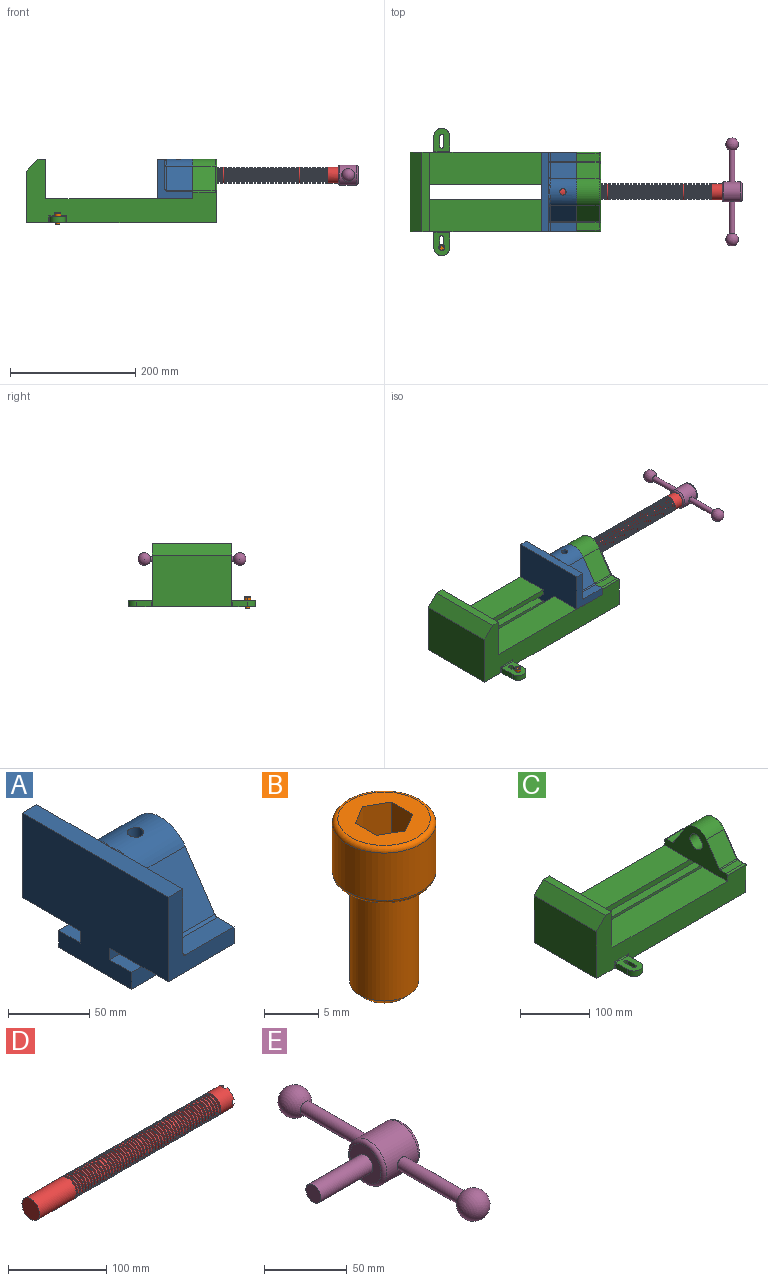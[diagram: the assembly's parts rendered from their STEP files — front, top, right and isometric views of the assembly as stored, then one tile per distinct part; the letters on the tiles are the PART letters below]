
ASSEMBLY  parts=5 mates=5
PART A: 36 faces, bbox 57.2x127x89 mm
  f0: plane 57.15x50.8mm, normal (0,0,-1), area 2903.2mm2, adj f6,f9,f10,f23
  f1: cylinder r=12.7mm len=44.45mm, axis (1,0,0), area 3464.3mm2, adj f6,f15,f16
  f2: plane 41.91x14.52mm, normal (0,0,1), area 608.5mm2, adj f6,f11,f24,f25
  f3: plane 51.86x48.26mm, normal (1,0,0), area 1495.7mm2, adj f8,f10,f31,f33,f35
  f4: plane 51.86x48.26mm, normal (1,0,0), area 1495.7mm2, adj f8,f11,f24,f28,f29
  f5: plane 57.15x50.8mm, normal (0,0,-1), area 2903.2mm2, adj f6,f9,f11,f22
  f6: plane 127x85.09mm, normal (1,0,0), area 5190.6mm2, adj f0,f1,f2,f5,f7,f10,f11,f12
  f7: plane 41.91x14.52mm, normal (0,0,1), area 608.5mm2, adj f6,f10,f30,f31
  f8: plane 127x12.7mm, normal (0,0,1), area 1612.9mm2, adj f3,f4,f9,f10,f11,f26,f34
  f9: plane 127x85.09mm, normal (-1,0,0), area 9096.8mm2, adj f0,f5,f8,f10,f11,f17,f18,f19
  f10: plane 63.5x57.15mm, normal (0,-1,0), area 1372.3mm2, adj f0,f3,f6,f7,f8,f9,f31
  f11: plane 63.5x57.15mm, normal (0,1,0), area 1372.3mm2, adj f2,f4,f5,f6,f8,f9,f24
  f12: plane 41.91x38.43mm, normal (0,-0.83,0.56), area 1939.2mm2, adj f6,f13,f30,f33
  f13: cylinder r=25.4mm len=44.45mm, axis (1,0,0), area 2026.5mm2, adj f6,f12,f14,f16,f26,f28,f34,f35
  f14: plane 41.91x38.43mm, normal (0,0.83,0.56), area 1939.2mm2, adj f6,f13,f25,f29
  f15: plane 25.4x25.4mm, normal (1,0,0), area 506.7mm2, adj f1
  f16: cylinder r=5.08mm len=13.76mm, axis (0,0,1), area 414mm2, adj f1,f13
  f17: plane 57.15x19.05mm, normal (0,0,1), area 1088.7mm2, adj f6,f9,f18,f23
  f18: plane 57.15x12.7mm, normal (0,-1,0), area 725.8mm2, adj f6,f9,f17,f19
  f19: plane 63.5x57.15mm, normal (0,0,-1), area 3629mm2, adj f6,f9,f18,f20
  f20: plane 57.15x12.7mm, normal (0,1,0), area 725.8mm2, adj f6,f9,f19,f21
  f21: plane 57.15x19.05mm, normal (0,0,1), area 1088.7mm2, adj f6,f9,f20,f22
  f22: plane 57.15x8.89mm, normal (0,1,0), area 508.1mm2, adj f5,f6,f9,f21
  f23: plane 57.15x8.89mm, normal (0,-1,0), area 508.1mm2, adj f0,f6,f9,f17
  f24: cylinder r=2.54mm len=14.52mm, axis (0,-1,0), area 57.9mm2, adj f2,f4,f11,f27
  f25: cylinder r=2.54mm len=41.91mm, axis (1,0,0), area 104.3mm2, adj f2,f6,f14,f27
  f26: bspline ~12.24x2.8mm, area 20.9mm2, adj f8,f13,f28
  f27: sphere r=2.54mm, area 6.3mm2, adj f24,f25,f29
  f28: torus R=27.94mm, axis (1,0,0), area 57.8mm2, adj f4,f13,f26,f29
  f29: cylinder r=2.54mm len=39.84mm, axis (0,-0.56,0.83), area 184.6mm2, adj f4,f14,f27,f28
  f30: cylinder r=2.54mm len=41.91mm, axis (1,0,0), area 104.3mm2, adj f6,f7,f12,f32
  f31: cylinder r=2.54mm len=14.52mm, axis (0,-1,0), area 57.9mm2, adj f3,f7,f10,f32
  f32: sphere r=2.54mm, area 6.3mm2, adj f30,f31,f33
  f33: cylinder r=2.54mm len=39.84mm, axis (0,-0.56,-0.83), area 184.6mm2, adj f3,f12,f32,f35
  f34: bspline ~12.24x2.8mm, area 20.9mm2, adj f8,f13,f35
  f35: torus R=27.94mm, axis (1,0,0), area 57.8mm2, adj f3,f13,f33,f34
PART B: 15 faces, bbox 10.3x10.3x19.1 mm
  f0: plane 8.51x8.51mm, normal (0,0,1), area 37.2mm2, adj f5,f6,f7,f8,f9,f10,f14
  f1: cylinder r=3.17mm len=11.94mm, axis (0,0,1), area 238.2mm2, adj f4,f12
  f2: plane 4.83x4.83mm, normal (0,0,-1), area 18.3mm2, adj f12
  f3: cylinder r=4.76mm len=9.53mm, axis (0,0,-1), area 159.6mm2, adj f13,f14
  f4: plane 8.51x8.51mm, normal (0,0,-1), area 25.2mm2, adj f1,f13
  f5: plane 4.83x2.38mm, normal (-0.5,-0.87,0), area 13.3mm2, adj f0,f6,f10,f11
  f6: plane 4.83x2.38mm, normal (0.5,-0.87,0), area 13.3mm2, adj f0,f5,f7,f11
  f7: plane 4.83x2.75mm, normal (1,0,0), area 13.3mm2, adj f0,f6,f8,f11
  f8: plane 4.83x2.38mm, normal (0.5,0.87,0), area 13.3mm2, adj f0,f7,f9,f11
  f9: plane 4.83x2.38mm, normal (-0.5,0.87,0), area 13.3mm2, adj f0,f8,f10,f11
  f10: plane 4.83x2.75mm, normal (-1,0,0), area 13.3mm2, adj f0,f5,f9,f11
  f11: plane 5.5x4.76mm, normal (0,0,1), area 19.6mm2, adj f5,f6,f7,f8,f9,f10
  f12: cone r=3.17mm half-angle=45deg, axis (0,0,1), area 18.9mm2, adj f1,f2
  f13: torus R=4.25mm, axis (0,0,1), area 23mm2, adj f3,f4
  f14: torus R=4.25mm, axis (0,0,1), area 23mm2, adj f0,f3
PART C: 61 faces, bbox 304.8x203.2x103.7 mm
  f0: plane 304.8x101.6mm, normal (0,1,0), area 13520.3mm2, adj f3,f4,f5,f6,f7,f8,f9,f16
  f1: plane 304.8x101.6mm, normal (0,-1,0), area 13520.3mm2, adj f2,f3,f5,f6,f7,f8,f9,f16
  f2: plane 234.95x50.8mm, normal (0,0,1), area 11935.5mm2, adj f1,f5,f16,f26
  f3: plane 127x99.06mm, normal (1,0,0), area 7097.5mm2, adj f0,f1,f9,f14,f17,f18,f19,f20
  f4: plane 234.95x50.8mm, normal (0,0,1), area 11935.5mm2, adj f0,f5,f16,f27
  f5: plane 127x101.6mm, normal (1,0,0), area 9516.1mm2, adj f0,f1,f2,f4,f6,f9,f18,f19
  f6: plane 127x12.7mm, normal (0,0,1), area 1612.9mm2, adj f0,f1,f5,f7
  f7: plane 127x19.05mm, normal (-0.71,0,0.71), area 3421.5mm2, adj f0,f1,f6,f8
  f8: plane 127x82.55mm, normal (-1,0,0), area 10483.8mm2, adj f0,f1,f7,f9
  f9: plane 304.8x203.2mm, normal (0,0,-1), area 33298.3mm2, adj f0,f1,f3,f5,f8,f21,f22,f39
  f10: plane 35.56x11.98mm, normal (0,0,1), area 426mm2, adj f16,f28,f29,f30
  f11: plane 38.43x35.56mm, normal (0,0.83,0.56), area 1645.4mm2, adj f12,f16,f29,f32
  f12: cylinder r=25.4mm len=42.19mm, axis (1,0,0), area 1770.2mm2, adj f11,f13,f16,f33
  f13: plane 38.43x35.56mm, normal (0,-0.83,0.56), area 1645.4mm2, adj f12,f16,f34,f35
  f14: cylinder r=12.7mm len=38.1mm, axis (1,0,0), area 3040.2mm2, adj f3,f16
  f15: plane 35.56x11.98mm, normal (0,0,1), area 426mm2, adj f16,f34,f36,f38
  f16: plane 127x63.5mm, normal (-1,0,0), area 4155.5mm2, adj f0,f1,f2,f4,f10,f11,f12,f13
  f17: plane 38.1x25.4mm, normal (0,0,-1), area 967.7mm2, adj f3,f16,f26,f27
  f18: plane 273.05x19.05mm, normal (0,0,-1), area 5201.6mm2, adj f3,f5,f19,f26
  f19: plane 273.05x12.7mm, normal (0,1,0), area 3467.7mm2, adj f3,f5,f18,f20
  f20: plane 273.05x19.05mm, normal (0,0,1), area 5201.6mm2, adj f3,f5,f19,f21
  f21: plane 273.05x16.51mm, normal (0,1,0), area 4508.1mm2, adj f3,f5,f9,f20
  f22: plane 273.05x16.51mm, normal (0,-1,0), area 4508.1mm2, adj f3,f5,f9,f23
  f23: plane 273.05x19.05mm, normal (0,0,1), area 5201.6mm2, adj f3,f5,f22,f24
  f24: plane 273.05x12.7mm, normal (0,-1,0), area 3467.7mm2, adj f3,f5,f23,f25
  f25: plane 273.05x19.05mm, normal (0,0,-1), area 5201.6mm2, adj f3,f5,f24,f27
  f26: plane 273.05x8.89mm, normal (0,1,0), area 2427.4mm2, adj f2,f3,f5,f17,f18
  f27: plane 273.05x8.89mm, normal (0,-1,0), area 2427.4mm2, adj f3,f4,f5,f17,f25
  f28: cylinder r=2.54mm len=38.1mm, axis (1,0,0), area 148.3mm2, adj f0,f10,f16,f30
  f29: cylinder r=2.54mm len=35.56mm, axis (-1,0,0), area 88.5mm2, adj f10,f11,f16,f31
  f30: cylinder r=2.54mm len=14.52mm, axis (0,1,0), area 54.3mm2, adj f3,f10,f28,f31
  f31: torus R=5.08mm, axis (-1,0,0), area 13.5mm2, adj f3,f29,f30,f32
  f32: cylinder r=2.54mm len=39.84mm, axis (0,0.56,-0.83), area 184.6mm2, adj f3,f11,f31,f33
  f33: torus R=22.86mm, axis (-1,0,0), area 191.4mm2, adj f3,f12,f32,f35
  f34: cylinder r=2.54mm len=35.56mm, axis (-1,0,0), area 88.5mm2, adj f13,f15,f16,f37
  f35: cylinder r=2.54mm len=39.84mm, axis (0,0.56,0.83), area 184.6mm2, adj f3,f13,f33,f37
  f36: cylinder r=2.54mm len=38.1mm, axis (-1,0,0), area 148.3mm2, adj f1,f15,f16,f38
  f37: torus R=5.08mm, axis (-1,0,0), area 13.5mm2, adj f3,f34,f35,f38
  f38: cylinder r=2.54mm len=14.52mm, axis (0,1,0), area 54.3mm2, adj f3,f15,f36,f37
  f39: plane 23.88x9.53mm, normal (-1,0,0), area 227.4mm2, adj f9,f45,f46,f60
  f40: plane 23.88x9.53mm, normal (1,0,0), area 227.4mm2, adj f9,f45,f46,f58
  f41: cylinder r=3.3mm len=9.53mm, axis (0,0,-1), area 98.8mm2, adj f9,f42,f44,f46
  f42: plane 15.62x9.53mm, normal (-1,0,0), area 148.8mm2, adj f9,f41,f43,f46
  f43: cylinder r=3.3mm len=9.53mm, axis (0,0,-1), area 98.8mm2, adj f9,f42,f44,f46
  f44: plane 15.62x9.53mm, normal (1,0,0), area 148.8mm2, adj f9,f41,f43,f46
  f45: cylinder r=12.7mm len=25.4mm, axis (0,0,-1), area 380mm2, adj f9,f39,f40,f46
  f46: plane 36.58x25.4mm, normal (0,0,1), area 722.4mm2, adj f39,f40,f41,f42,f43,f44,f45,f59
  f47: plane 23.88x9.53mm, normal (-1,0,0), area 227.4mm2, adj f9,f53,f54,f56
  f48: plane 23.88x9.53mm, normal (1,0,0), area 227.4mm2, adj f9,f53,f54,f55
  f49: cylinder r=3.3mm len=9.53mm, axis (0,0,-1), area 98.8mm2, adj f9,f50,f52,f54
  f50: plane 15.62x9.53mm, normal (-1,0,0), area 148.8mm2, adj f9,f49,f51,f54
  f51: cylinder r=3.3mm len=9.53mm, axis (0,0,-1), area 98.8mm2, adj f9,f50,f52,f54
  f52: plane 15.62x9.53mm, normal (1,0,0), area 148.8mm2, adj f9,f49,f51,f54
  f53: cylinder r=12.7mm len=25.4mm, axis (0,0,-1), area 380mm2, adj f9,f47,f48,f54
  f54: plane 36.58x25.4mm, normal (0,0,1), area 722.4mm2, adj f47,f48,f49,f50,f51,f52,f53,f57
  f55: cylinder r=1.52mm len=11.05mm, axis (0,0,-1), area 24.1mm2, adj f0,f9,f48,f57
  f56: cylinder r=1.52mm len=11.05mm, axis (0,0,1), area 24.1mm2, adj f0,f9,f47,f57
  f57: cylinder r=1.52mm len=28.45mm, axis (1,0,0), area 63.5mm2, adj f0,f54,f55,f56
  f58: cylinder r=1.52mm len=11.05mm, axis (0,0,1), area 24.1mm2, adj f1,f9,f40,f59
  f59: cylinder r=1.52mm len=28.45mm, axis (-1,0,0), area 63.5mm2, adj f1,f46,f58,f60
  f60: cylinder r=1.52mm len=11.05mm, axis (0,0,-1), area 24.1mm2, adj f1,f9,f39,f59
PART D: 220 faces, bbox 279.4x25.4x25.4 mm
  f0: cylinder r=12.7mm len=25.4mm, axis (-1,0,0), area 1468.2mm2, adj f1,f2,f3,f5,f7,f208,f209,f210
  f1: plane 9.9x9.9mm, normal (1,0,0), area 62.3mm2, adj f0,f4,f213,f216
  f2: plane 9.9x9.9mm, normal (1,0,0), area 62.3mm2, adj f0,f4,f210,f218
  f3: plane 9.9x9.9mm, normal (1,0,0), area 62.3mm2, adj f0,f4,f209,f212
  f4: cylinder r=6.35mm len=25.4mm, axis (1,0,0), area 960.3mm2, adj f1,f2,f3,f5,f6,f208,f209,f210
  f5: plane 9.9x9.9mm, normal (1,0,0), area 62.3mm2, adj f0,f4,f215,f217
  f6: plane 12.7x12.7mm, normal (1,0,0), area 126.7mm2, adj f4
  f7: cone r=12.7mm half-angle=76deg, axis (1,0,0), area 188mm2, adj f0,f9
  f8: cone r=10.16mm half-angle=76deg, axis (-1,0,0), area 188mm2, adj f9,f10
  f9: cylinder r=10.16mm len=20.32mm, axis (1,0,0), area 81.1mm2, adj f7,f8
  f10: cylinder r=12.7mm len=25.4mm, axis (-1,0,0), area 131.7mm2, adj f8,f11
  f11: cone r=12.7mm half-angle=76deg, axis (1,0,0), area 188mm2, adj f10,f13
  f12: cone r=10.16mm half-angle=76deg, axis (-1,0,0), area 188mm2, adj f13,f14
  f13: cylinder r=10.16mm len=20.32mm, axis (1,0,0), area 81.1mm2, adj f11,f12
  f14: cylinder r=12.7mm len=25.4mm, axis (-1,0,0), area 131.7mm2, adj f12,f15
  f15: cone r=12.7mm half-angle=76deg, axis (1,0,0), area 188mm2, adj f14,f17
  f16: cone r=10.16mm half-angle=76deg, axis (-1,0,0), area 188mm2, adj f17,f18
  f17: cylinder r=10.16mm len=20.32mm, axis (1,0,0), area 81.1mm2, adj f15,f16
  f18: cylinder r=12.7mm len=25.4mm, axis (-1,0,0), area 131.7mm2, adj f16,f19
  f19: cone r=12.7mm half-angle=76deg, axis (1,0,0), area 188mm2, adj f18,f21
  f20: cone r=10.16mm half-angle=76deg, axis (-1,0,0), area 188mm2, adj f21,f22
  f21: cylinder r=10.16mm len=20.32mm, axis (1,0,0), area 81.1mm2, adj f19,f20
  f22: cylinder r=12.7mm len=25.4mm, axis (-1,0,0), area 131.7mm2, adj f20,f23
  f23: cone r=12.7mm half-angle=76deg, axis (1,0,0), area 188mm2, adj f22,f25
  f24: cone r=10.16mm half-angle=76deg, axis (-1,0,0), area 188mm2, adj f25,f26
  f25: cylinder r=10.16mm len=20.32mm, axis (1,0,0), area 81.1mm2, adj f23,f24
  f26: cylinder r=12.7mm len=25.4mm, axis (-1,0,0), area 131.7mm2, adj f24,f27
  f27: cone r=12.7mm half-angle=76deg, axis (1,0,0), area 188mm2, adj f26,f29
  f28: cone r=10.16mm half-angle=76deg, axis (-1,0,0), area 188mm2, adj f29,f30
  f29: cylinder r=10.16mm len=20.32mm, axis (1,0,0), area 81.1mm2, adj f27,f28
  f30: cylinder r=12.7mm len=25.4mm, axis (-1,0,0), area 131.7mm2, adj f28,f31
  f31: cone r=12.7mm half-angle=76deg, axis (1,0,0), area 188mm2, adj f30,f33
  f32: cone r=10.16mm half-angle=76deg, axis (-1,0,0), area 188mm2, adj f33,f34
  f33: cylinder r=10.16mm len=20.32mm, axis (1,0,0), area 81.1mm2, adj f31,f32
  f34: cylinder r=12.7mm len=25.4mm, axis (-1,0,0), area 131.7mm2, adj f32,f35
  f35: cone r=12.7mm half-angle=76deg, axis (1,0,0), area 188mm2, adj f34,f37
  f36: cone r=10.16mm half-angle=76deg, axis (-1,0,0), area 188mm2, adj f37,f38
  f37: cylinder r=10.16mm len=20.32mm, axis (1,0,0), area 81.1mm2, adj f35,f36
  f38: cylinder r=12.7mm len=25.4mm, axis (-1,0,0), area 131.7mm2, adj f36,f39
  f39: cone r=12.7mm half-angle=76deg, axis (1,0,0), area 188mm2, adj f38,f41
  f40: cone r=10.16mm half-angle=76deg, axis (-1,0,0), area 188mm2, adj f41,f42
  f41: cylinder r=10.16mm len=20.32mm, axis (1,0,0), area 81.1mm2, adj f39,f40
  f42: cylinder r=12.7mm len=25.4mm, axis (-1,0,0), area 131.7mm2, adj f40,f43
  f43: cone r=12.7mm half-angle=76deg, axis (1,0,0), area 188mm2, adj f42,f45
  f44: cone r=10.16mm half-angle=76deg, axis (-1,0,0), area 188mm2, adj f45,f46
  f45: cylinder r=10.16mm len=20.32mm, axis (1,0,0), area 81.1mm2, adj f43,f44
  f46: cylinder r=12.7mm len=25.4mm, axis (-1,0,0), area 131.7mm2, adj f44,f47
  f47: cone r=12.7mm half-angle=76deg, axis (1,0,0), area 188mm2, adj f46,f49
  f48: cone r=10.16mm half-angle=76deg, axis (-1,0,0), area 188mm2, adj f49,f50
  f49: cylinder r=10.16mm len=20.32mm, axis (1,0,0), area 81.1mm2, adj f47,f48
  f50: cylinder r=12.7mm len=25.4mm, axis (-1,0,0), area 131.7mm2, adj f48,f51
  f51: cone r=12.7mm half-angle=76deg, axis (1,0,0), area 188mm2, adj f50,f53
  f52: cone r=10.16mm half-angle=76deg, axis (-1,0,0), area 188mm2, adj f53,f54
  f53: cylinder r=10.16mm len=20.32mm, axis (1,0,0), area 81.1mm2, adj f51,f52
  f54: cylinder r=12.7mm len=25.4mm, axis (-1,0,0), area 131.7mm2, adj f52,f55
  f55: cone r=12.7mm half-angle=76deg, axis (1,0,0), area 188mm2, adj f54,f57
  f56: cone r=10.16mm half-angle=76deg, axis (-1,0,0), area 188mm2, adj f57,f58
  f57: cylinder r=10.16mm len=20.32mm, axis (1,0,0), area 81.1mm2, adj f55,f56
  f58: cylinder r=12.7mm len=25.4mm, axis (-1,0,0), area 131.7mm2, adj f56,f59
  f59: cone r=12.7mm half-angle=76deg, axis (1,0,0), area 188mm2, adj f58,f61
  f60: cone r=10.16mm half-angle=76deg, axis (-1,0,0), area 188mm2, adj f61,f62
  f61: cylinder r=10.16mm len=20.32mm, axis (1,0,0), area 81.1mm2, adj f59,f60
  f62: cylinder r=12.7mm len=25.4mm, axis (-1,0,0), area 131.7mm2, adj f60,f63
  f63: cone r=12.7mm half-angle=76deg, axis (1,0,0), area 188mm2, adj f62,f65
  f64: cone r=10.16mm half-angle=76deg, axis (-1,0,0), area 188mm2, adj f65,f66
  f65: cylinder r=10.16mm len=20.32mm, axis (1,0,0), area 81.1mm2, adj f63,f64
  f66: cylinder r=12.7mm len=25.4mm, axis (-1,0,0), area 131.7mm2, adj f64,f67
  f67: cone r=12.7mm half-angle=76deg, axis (1,0,0), area 188mm2, adj f66,f69
  f68: cone r=10.16mm half-angle=76deg, axis (-1,0,0), area 188mm2, adj f69,f70
  f69: cylinder r=10.16mm len=20.32mm, axis (1,0,0), area 81.1mm2, adj f67,f68
  f70: cylinder r=12.7mm len=25.4mm, axis (-1,0,0), area 131.7mm2, adj f68,f71
  f71: cone r=12.7mm half-angle=76deg, axis (1,0,0), area 188mm2, adj f70,f73
  f72: cone r=10.16mm half-angle=76deg, axis (-1,0,0), area 188mm2, adj f73,f74
  f73: cylinder r=10.16mm len=20.32mm, axis (1,0,0), area 81.1mm2, adj f71,f72
  f74: cylinder r=12.7mm len=25.4mm, axis (-1,0,0), area 131.7mm2, adj f72,f75
  f75: cone r=12.7mm half-angle=76deg, axis (1,0,0), area 188mm2, adj f74,f77
  f76: cone r=10.16mm half-angle=76deg, axis (-1,0,0), area 188mm2, adj f77,f78
  f77: cylinder r=10.16mm len=20.32mm, axis (1,0,0), area 81.1mm2, adj f75,f76
  f78: cylinder r=12.7mm len=25.4mm, axis (-1,0,0), area 131.7mm2, adj f76,f79
  f79: cone r=12.7mm half-angle=76deg, axis (1,0,0), area 188mm2, adj f78,f81
  f80: cone r=10.16mm half-angle=76deg, axis (-1,0,0), area 188mm2, adj f81,f82
  f81: cylinder r=10.16mm len=20.32mm, axis (1,0,0), area 81.1mm2, adj f79,f80
  f82: cylinder r=12.7mm len=25.4mm, axis (-1,0,0), area 131.7mm2, adj f80,f83
  f83: cone r=12.7mm half-angle=76deg, axis (1,0,0), area 188mm2, adj f82,f85
  f84: cone r=10.16mm half-angle=76deg, axis (-1,0,0), area 188mm2, adj f85,f86
  f85: cylinder r=10.16mm len=20.32mm, axis (1,0,0), area 81.1mm2, adj f83,f84
  f86: cylinder r=12.7mm len=25.4mm, axis (-1,0,0), area 131.7mm2, adj f84,f87
  f87: cone r=12.7mm half-angle=76deg, axis (1,0,0), area 188mm2, adj f86,f89
  f88: cone r=10.16mm half-angle=76deg, axis (-1,0,0), area 188mm2, adj f89,f90
  f89: cylinder r=10.16mm len=20.32mm, axis (1,0,0), area 81.1mm2, adj f87,f88
  f90: cylinder r=12.7mm len=25.4mm, axis (-1,0,0), area 131.7mm2, adj f88,f91
  f91: cone r=12.7mm half-angle=76deg, axis (1,0,0), area 188mm2, adj f90,f93
  f92: cone r=10.16mm half-angle=76deg, axis (-1,0,0), area 188mm2, adj f93,f94
  f93: cylinder r=10.16mm len=20.32mm, axis (1,0,0), area 81.1mm2, adj f91,f92
  f94: cylinder r=12.7mm len=25.4mm, axis (-1,0,0), area 131.7mm2, adj f92,f95
  f95: cone r=12.7mm half-angle=76deg, axis (1,0,0), area 188mm2, adj f94,f97
  f96: cone r=10.16mm half-angle=76deg, axis (-1,0,0), area 188mm2, adj f97,f98
  f97: cylinder r=10.16mm len=20.32mm, axis (1,0,0), area 81.1mm2, adj f95,f96
  f98: cylinder r=12.7mm len=25.4mm, axis (-1,0,0), area 131.7mm2, adj f96,f99
  f99: cone r=12.7mm half-angle=76deg, axis (1,0,0), area 188mm2, adj f98,f101
  f100: cone r=10.16mm half-angle=76deg, axis (-1,0,0), area 188mm2, adj f101,f102
  f101: cylinder r=10.16mm len=20.32mm, axis (1,0,0), area 81.1mm2, adj f99,f100
  f102: cylinder r=12.7mm len=25.4mm, axis (-1,0,0), area 131.7mm2, adj f100,f103
  f103: cone r=12.7mm half-angle=76deg, axis (1,0,0), area 188mm2, adj f102,f105
  f104: cone r=10.16mm half-angle=76deg, axis (-1,0,0), area 188mm2, adj f105,f106
  f105: cylinder r=10.16mm len=20.32mm, axis (1,0,0), area 81.1mm2, adj f103,f104
  f106: cylinder r=12.7mm len=25.4mm, axis (-1,0,0), area 131.7mm2, adj f104,f107
  f107: cone r=12.7mm half-angle=76deg, axis (1,0,0), area 188mm2, adj f106,f109
  f108: cone r=10.16mm half-angle=76deg, axis (-1,0,0), area 188mm2, adj f109,f110
  f109: cylinder r=10.16mm len=20.32mm, axis (1,0,0), area 81.1mm2, adj f107,f108
  f110: cylinder r=12.7mm len=25.4mm, axis (-1,0,0), area 131.7mm2, adj f108,f111
  f111: cone r=12.7mm half-angle=76deg, axis (1,0,0), area 188mm2, adj f110,f113
  f112: cone r=10.16mm half-angle=76deg, axis (-1,0,0), area 188mm2, adj f113,f114
  f113: cylinder r=10.16mm len=20.32mm, axis (1,0,0), area 81.1mm2, adj f111,f112
  f114: cylinder r=12.7mm len=25.4mm, axis (-1,0,0), area 131.7mm2, adj f112,f115
  f115: cone r=12.7mm half-angle=76deg, axis (1,0,0), area 188mm2, adj f114,f117
  f116: cone r=10.16mm half-angle=76deg, axis (-1,0,0), area 188mm2, adj f117,f118
  f117: cylinder r=10.16mm len=20.32mm, axis (1,0,0), area 81.1mm2, adj f115,f116
  f118: cylinder r=12.7mm len=25.4mm, axis (-1,0,0), area 131.7mm2, adj f116,f119
  f119: cone r=12.7mm half-angle=76deg, axis (1,0,0), area 188mm2, adj f118,f121
  f120: cone r=10.16mm half-angle=76deg, axis (-1,0,0), area 188mm2, adj f121,f122
  f121: cylinder r=10.16mm len=20.32mm, axis (1,0,0), area 81.1mm2, adj f119,f120
  f122: cylinder r=12.7mm len=25.4mm, axis (-1,0,0), area 131.7mm2, adj f120,f123
  f123: cone r=12.7mm half-angle=76deg, axis (1,0,0), area 188mm2, adj f122,f125
  f124: cone r=10.16mm half-angle=76deg, axis (-1,0,0), area 188mm2, adj f125,f126
  f125: cylinder r=10.16mm len=20.32mm, axis (1,0,0), area 81.1mm2, adj f123,f124
  f126: cylinder r=12.7mm len=25.4mm, axis (-1,0,0), area 131.7mm2, adj f124,f127
  f127: cone r=12.7mm half-angle=76deg, axis (1,0,0), area 188mm2, adj f126,f129
  f128: cone r=10.16mm half-angle=76deg, axis (-1,0,0), area 188mm2, adj f129,f130
  f129: cylinder r=10.16mm len=20.32mm, axis (1,0,0), area 81.1mm2, adj f127,f128
  f130: cylinder r=12.7mm len=25.4mm, axis (-1,0,0), area 131.7mm2, adj f128,f131
  f131: cone r=12.7mm half-angle=76deg, axis (1,0,0), area 188mm2, adj f130,f133
  f132: cone r=10.16mm half-angle=76deg, axis (-1,0,0), area 188mm2, adj f133,f134
  f133: cylinder r=10.16mm len=20.32mm, axis (1,0,0), area 81.1mm2, adj f131,f132
  f134: cylinder r=12.7mm len=25.4mm, axis (-1,0,0), area 131.7mm2, adj f132,f135
  f135: cone r=12.7mm half-angle=76deg, axis (1,0,0), area 188mm2, adj f134,f137
  f136: cone r=10.16mm half-angle=76deg, axis (-1,0,0), area 188mm2, adj f137,f138
  f137: cylinder r=10.16mm len=20.32mm, axis (1,0,0), area 81.1mm2, adj f135,f136
  f138: cylinder r=12.7mm len=25.4mm, axis (-1,0,0), area 131.7mm2, adj f136,f139
  f139: cone r=12.7mm half-angle=76deg, axis (1,0,0), area 188mm2, adj f138,f141
  f140: cone r=10.16mm half-angle=76deg, axis (-1,0,0), area 188mm2, adj f141,f142
  f141: cylinder r=10.16mm len=20.32mm, axis (1,0,0), area 81.1mm2, adj f139,f140
  f142: cylinder r=12.7mm len=25.4mm, axis (-1,0,0), area 131.7mm2, adj f140,f143
  f143: cone r=12.7mm half-angle=76deg, axis (1,0,0), area 188mm2, adj f142,f145
  f144: cone r=10.16mm half-angle=76deg, axis (-1,0,0), area 188mm2, adj f145,f146
  f145: cylinder r=10.16mm len=20.32mm, axis (1,0,0), area 81.1mm2, adj f143,f144
  f146: cylinder r=12.7mm len=25.4mm, axis (-1,0,0), area 131.7mm2, adj f144,f147
  f147: cone r=12.7mm half-angle=76deg, axis (1,0,0), area 188mm2, adj f146,f149
  f148: cone r=10.16mm half-angle=76deg, axis (-1,0,0), area 188mm2, adj f149,f150
  f149: cylinder r=10.16mm len=20.32mm, axis (1,0,0), area 81.1mm2, adj f147,f148
  f150: cylinder r=12.7mm len=25.4mm, axis (-1,0,0), area 131.7mm2, adj f148,f151
  f151: cone r=12.7mm half-angle=76deg, axis (1,0,0), area 188mm2, adj f150,f153
  f152: cone r=10.16mm half-angle=76deg, axis (-1,0,0), area 188mm2, adj f153,f154
  f153: cylinder r=10.16mm len=20.32mm, axis (1,0,0), area 81.1mm2, adj f151,f152
  f154: cylinder r=12.7mm len=25.4mm, axis (-1,0,0), area 131.7mm2, adj f152,f155
  f155: cone r=12.7mm half-angle=76deg, axis (1,0,0), area 188mm2, adj f154,f157
  f156: cone r=10.16mm half-angle=76deg, axis (-1,0,0), area 188mm2, adj f157,f158
  f157: cylinder r=10.16mm len=20.32mm, axis (1,0,0), area 81.1mm2, adj f155,f156
  f158: cylinder r=12.7mm len=25.4mm, axis (-1,0,0), area 131.7mm2, adj f156,f159
  f159: cone r=12.7mm half-angle=76deg, axis (1,0,0), area 188mm2, adj f158,f161
  f160: cone r=10.16mm half-angle=76deg, axis (-1,0,0), area 188mm2, adj f161,f162
  f161: cylinder r=10.16mm len=20.32mm, axis (1,0,0), area 81.1mm2, adj f159,f160
  f162: cylinder r=12.7mm len=25.4mm, axis (-1,0,0), area 131.7mm2, adj f160,f163
  f163: cone r=12.7mm half-angle=76deg, axis (1,0,0), area 188mm2, adj f162,f165
  f164: cone r=10.16mm half-angle=76deg, axis (-1,0,0), area 188mm2, adj f165,f166
  f165: cylinder r=10.16mm len=20.32mm, axis (1,0,0), area 81.1mm2, adj f163,f164
  f166: cylinder r=12.7mm len=25.4mm, axis (-1,0,0), area 131.7mm2, adj f164,f167
  f167: cone r=12.7mm half-angle=76deg, axis (1,0,0), area 188mm2, adj f166,f169
  f168: cone r=10.16mm half-angle=76deg, axis (-1,0,0), area 188mm2, adj f169,f170
  f169: cylinder r=10.16mm len=20.32mm, axis (1,0,0), area 81.1mm2, adj f167,f168
  f170: cylinder r=12.7mm len=25.4mm, axis (-1,0,0), area 131.7mm2, adj f168,f171
  f171: cone r=12.7mm half-angle=76deg, axis (1,0,0), area 188mm2, adj f170,f173
  f172: cone r=10.16mm half-angle=76deg, axis (-1,0,0), area 188mm2, adj f173,f174
  f173: cylinder r=10.16mm len=20.32mm, axis (1,0,0), area 81.1mm2, adj f171,f172
  f174: cylinder r=12.7mm len=25.4mm, axis (-1,0,0), area 131.7mm2, adj f172,f175
  f175: cone r=12.7mm half-angle=76deg, axis (1,0,0), area 188mm2, adj f174,f177
  f176: cone r=10.16mm half-angle=76deg, axis (-1,0,0), area 188mm2, adj f177,f178
  f177: cylinder r=10.16mm len=20.32mm, axis (1,0,0), area 81.1mm2, adj f175,f176
  f178: cylinder r=12.7mm len=25.4mm, axis (-1,0,0), area 131.7mm2, adj f176,f179
  f179: cone r=12.7mm half-angle=76deg, axis (1,0,0), area 188mm2, adj f178,f181
  f180: cone r=10.16mm half-angle=76deg, axis (-1,0,0), area 188mm2, adj f181,f182
  f181: cylinder r=10.16mm len=20.32mm, axis (1,0,0), area 81.1mm2, adj f179,f180
  f182: cylinder r=12.7mm len=25.4mm, axis (-1,0,0), area 131.7mm2, adj f180,f183
  f183: cone r=12.7mm half-angle=76deg, axis (1,0,0), area 188mm2, adj f182,f185
  f184: cone r=10.16mm half-angle=76deg, axis (-1,0,0), area 188mm2, adj f185,f186
  f185: cylinder r=10.16mm len=20.32mm, axis (1,0,0), area 81.1mm2, adj f183,f184
  f186: cylinder r=12.7mm len=25.4mm, axis (-1,0,0), area 131.7mm2, adj f184,f187
  f187: cone r=12.7mm half-angle=76deg, axis (1,0,0), area 188mm2, adj f186,f189
  f188: cone r=10.16mm half-angle=76deg, axis (-1,0,0), area 188mm2, adj f189,f190
  f189: cylinder r=10.16mm len=20.32mm, axis (1,0,0), area 81.1mm2, adj f187,f188
  f190: cylinder r=12.7mm len=25.4mm, axis (-1,0,0), area 131.7mm2, adj f188,f191
  f191: cone r=12.7mm half-angle=76deg, axis (1,0,0), area 188mm2, adj f190,f193
  f192: cone r=10.16mm half-angle=76deg, axis (-1,0,0), area 188mm2, adj f193,f194
  f193: cylinder r=10.16mm len=20.32mm, axis (1,0,0), area 81.1mm2, adj f191,f192
  f194: cylinder r=12.7mm len=25.4mm, axis (-1,0,0), area 131.7mm2, adj f192,f195
  f195: cone r=12.7mm half-angle=76deg, axis (1,0,0), area 188mm2, adj f194,f197
  f196: cone r=10.16mm half-angle=76deg, axis (-1,0,0), area 188mm2, adj f197,f198
  f197: cylinder r=10.16mm len=20.32mm, axis (1,0,0), area 81.1mm2, adj f195,f196
  f198: cylinder r=12.7mm len=25.4mm, axis (-1,0,0), area 131.7mm2, adj f196,f199
  f199: cone r=12.7mm half-angle=76deg, axis (1,0,0), area 188mm2, adj f198,f201
  f200: cone r=10.16mm half-angle=76deg, axis (-1,0,0), area 188mm2, adj f201,f202
  f201: cylinder r=10.16mm len=20.32mm, axis (1,0,0), area 81.1mm2, adj f199,f200
  f202: cylinder r=12.7mm len=25.4mm, axis (-1,0,0), area 131.7mm2, adj f200,f203
  f203: cone r=12.7mm half-angle=76deg, axis (1,0,0), area 188mm2, adj f202,f205
  f204: cone r=10.16mm half-angle=76deg, axis (-1,0,0), area 188mm2, adj f205,f207
  f205: cylinder r=10.16mm len=20.32mm, axis (1,0,0), area 81.1mm2, adj f203,f204
  f206: plane 25.4x25.4mm, normal (-1,0,0), area 506.7mm2, adj f207
  f207: cylinder r=12.7mm len=52.45mm, axis (-1,0,0), area 4185.4mm2, adj f204,f206
  f208: plane 6.88x5.08mm, normal (1,0,0), area 32.7mm2, adj f0,f4,f209,f210
  f209: plane 6.62x2.54mm, normal (0,-1,0), area 16.8mm2, adj f0,f3,f4,f208
  f210: plane 6.62x2.54mm, normal (0,1,0), area 16.8mm2, adj f0,f2,f4,f208
  f211: plane 6.88x5.08mm, normal (1,0,0), area 32.7mm2, adj f0,f4,f212,f213
  f212: plane 6.62x2.54mm, normal (0,0,1), area 16.8mm2, adj f0,f3,f4,f211
  f213: plane 6.62x2.54mm, normal (0,0,-1), area 16.8mm2, adj f0,f1,f4,f211
  f214: plane 6.88x5.08mm, normal (1,0,0), area 32.7mm2, adj f0,f4,f215,f216
  f215: plane 6.62x2.54mm, normal (0,1,0), area 16.8mm2, adj f0,f4,f5,f214
  f216: plane 6.62x2.54mm, normal (0,-1,0), area 16.8mm2, adj f0,f1,f4,f214
  f217: plane 6.62x2.54mm, normal (0,0,-1), area 16.8mm2, adj f0,f4,f5,f219
  f218: plane 6.62x2.54mm, normal (0,0,1), area 16.8mm2, adj f0,f2,f4,f219
  f219: plane 6.88x5.08mm, normal (1,0,0), area 32.7mm2, adj f0,f4,f217,f218
PART E: 11 faces, bbox 76.2x172.7x34.4 mm
  f0: sphere r=10.16mm, area 1231.8mm2, adj f1
  f1: cylinder r=4.45mm len=51.82mm, axis (0,1,0), area 1438.5mm2, adj f0,f4
  f2: sphere r=10.16mm, area 1231.8mm2, adj f3
  f3: cylinder r=4.45mm len=51.82mm, axis (0,1,0), area 1438.5mm2, adj f2,f4
  f4: cylinder r=15.88mm len=31.75mm, axis (-1,0,0), area 2534.7mm2, adj f1,f3,f9,f10
  f5: cylinder r=6.35mm len=44.45mm, axis (-1,0,0), area 1773.5mm2, adj f6,f8
  f6: plane 12.7x12.7mm, normal (-1,0,0), area 126.7mm2, adj f5
  f7: plane 26.67x26.67mm, normal (1,0,0), area 558.6mm2, adj f10
  f8: plane 26.67x26.67mm, normal (-1,0,0), area 432mm2, adj f5,f9
  f9: torus R=13.33mm, axis (1,0,0), area 374.8mm2, adj f4,f8
  f10: torus R=13.33mm, axis (1,0,0), area 374.8mm2, adj f4,f7
PLACE A t=(177.8,0,0)mm
PLACE B rot(axis=(0,0,1),90deg) t=(-254,-88.9,9.52)mm
PLACE C at identity fixed
PLACE D rot(axis=(-1,0,0),180deg) t=(177.8,0,152.4)mm
PLACE E rot(axis=(1,0,0),180deg) t=(156.21,0,152.4)mm
MATE fastened D.f4 <-> E.f5  axis (1,0,0) through (194.31,0,76.2)mm
MATE planar A.f0 <-> C.f2  axis (0,0,-1) through (-66.68,-38.1,38.1)mm
MATE pin_slot B.f1 <-> C.f41  axis (0,0,1) through (-254,-88.9,9.52)mm
MATE revolute D.f7 <-> A.f28  axis (-1,0,0) through (-82.55,0,76.2)mm
MATE cylindrical C.f12 <-> D.f7  axis (-1,0,0) through (-38.1,0,76.2)mm
